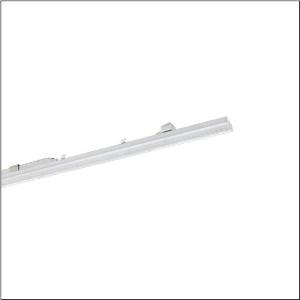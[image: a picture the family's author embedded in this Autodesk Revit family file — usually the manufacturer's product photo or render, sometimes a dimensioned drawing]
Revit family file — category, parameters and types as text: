
# Revit family: tl_l_5wd7a8f0h2c5
name_source: partatom
category: Lighting Fixtures
units: mm (PartAtom-declared; Revit-internal decimal feet)

## family parameters
Cut with Voids When Loaded = No
Host = Face
Light Source = No
Part Type = Normal
Room Calculation Point = No
Round Connector Dimension = Use Diameter
Shared = No

## types (1)
- TL L (1 x LED, 9800 lm, 63.3 W, 4000K)
    Apparent Load = 63 VA
    CIE Flux Codes = 49 84 98 100 100
    Color Rendering = 80
    Color Temperature = 4000K
    Default Elevation = 1800 mm
    Description = TL L, luminaire insert, of sheet steel, galvanised, coil coated, white, length: 1.500mm, width: 66mm, height: 67mm, surge protection,LED rated luminous flux: 9.800lm, light colour: 840, control gear: 4..20mA, with terminal, 5-pole, mains connection: 230..240V, AC, 50/60Hz, rated input power: 63W, micro fuse,primary optical cover: cover, of PMMA, light emission: direct distribution, protection rating (complete): as luminaire, insulation class (complete): insulation class I (protective earthing), certification: CE, impact resistance: IK06, permissible ambient temperature for indoor applications: -25..+35°C, packaging unit: 1 piece
    Height = 120 mm
    Lamp = 1 x LED
    Lamp Light Flux = 9800 lm
    Lamp Power = 63.3 W
    Lamp count = 1
    Length = 1690 mm
    Luminous efficacy = 155 lm/W
    Manufacturer = Siteco
    ModVariant = No
    Model = 5WD7A8F0H2C5
    Mounting Place = Ceiling
    Mounting Type = Pendant
    Number of Poles = 1
    OnlyDefault = Yes
    Power Factor = 1
    Product Name = TL L
    Product group = luminaire insert
    ProductGroupID = 901
    Protection Class = Protection class I
    Protection Degree = Degree of protection
    RLX_Detail_Level = 1
    RLX_Emergency_Light_Flux = 0 lm
    RLX_Emergency_Type = 0
    RLX_Emergency_Type_DB = No
    RlxData = <blob elided: 14169 chars, md5=624f0a04>
    Socket = socket
    Standby Power = 0 W
    System Light Flux = 9800 lm
    System Power = 63 W
    Type Comments = Product without accessories
    Type Image = l_1294382.jpg
    URL = http://relux.com
    VarID = ---
    Voltage = 0 V
    Weight = 0.00 kg
    Width = 208 mm

## geometry (parser evidence)
native form markers: Sweep x11
no freeform markers — native parametric forms only
